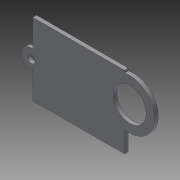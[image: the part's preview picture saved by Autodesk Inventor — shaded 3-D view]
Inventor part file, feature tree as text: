
AUTODESK INVENTOR PART (.ipt)
format: ipt  version: 2015 (Build 190159000, 159)  size: 93,696 bytes
history: native  units: mm
features: extrude x1, sketch x1
ambient origin geometry x8: Origin, YZ Plane, XZ Plane, XY Plane, X Axis, Y Axis, Z Axis, Center Point
bodies: Solid2 (feature_tree)
feature tree (2):
  extrude  "Extrusion1"  Depth=73.5mm
  sketch  "Sketch1"  dims[d0=58.0mm d1=73.5mm d7=6.5mm d8=40.0mm d9=26.5mm d10=3.0mm d11=0.0mm]
